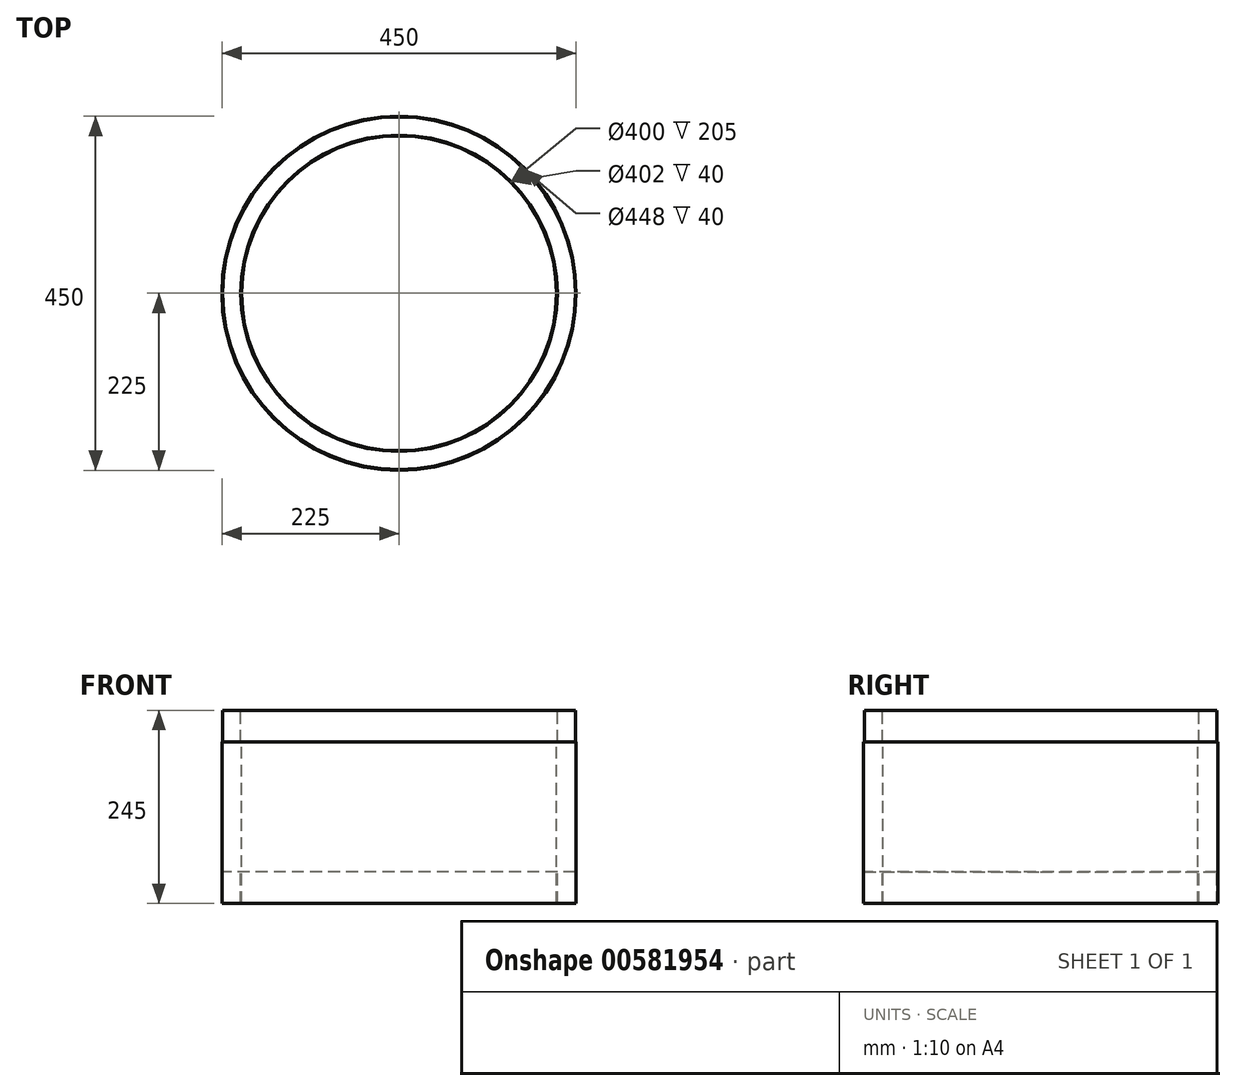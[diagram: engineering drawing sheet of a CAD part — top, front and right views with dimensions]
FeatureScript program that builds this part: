
annotation { "Feature Type Name" : "Feature", "Feature Type Description" : "" }
export const myFeature = defineFeature(function(context is Context, id is Id, definition is map)
    precondition{}
    {
        {
            var Q0;
            Q0=qCreatedBy(makeId("Front.planeOp"),FACE);
            var sketch = newSketch(context, id + "F0", { "sketchPlane" : qUnion([Q0])});
            skLineSegment(sketch, "E0", {"start": v(0, 345.75) * mm, "end": v(0, -558.03) * mm, "construction": true});
            skLineSegment(sketch, "E1", {"start": v(-200, -518.84) * mm, "end": v(-200, -313.84) * mm});
            skLineSegment(sketch, "E2", {"start": v(-200, -313.84) * mm, "end": v(-201, -313.84) * mm});
            skLineSegment(sketch, "E3", {"start": v(-201, -313.84) * mm, "end": v(-201, -273.84) * mm});
            skLineSegment(sketch, "E4", {"start": v(-201, -273.84) * mm, "end": v(-224, -273.84) * mm});
            skLineSegment(sketch, "E5", {"start": v(-224, -273.84) * mm, "end": v(-224, -313.84) * mm});
            skLineSegment(sketch, "E6", {"start": v(-224, -313.84) * mm, "end": v(-225, -313.84) * mm});
            skLineSegment(sketch, "E7", {"start": v(-225, -313.84) * mm, "end": v(-225, -518.84) * mm});
            skLineSegment(sketch, "E8", {"start": v(-225, -518.84) * mm, "end": v(-224, -518.84) * mm});
            skLineSegment(sketch, "E9", {"start": v(-224, -518.84) * mm, "end": v(-224, -478.84) * mm});
            skLineSegment(sketch, "E10", {"start": v(-224, -478.84) * mm, "end": v(-201, -478.84) * mm});
            skLineSegment(sketch, "E11", {"start": v(-201, -478.84) * mm, "end": v(-201, -518.84) * mm});
            skLineSegment(sketch, "E12", {"start": v(-201, -518.84) * mm, "end": v(-200, -518.84) * mm});
            skSolve(sketch);
        }
        {
            var Q0;
            Q0=qSketchRegion(id+"F0",true);
            var Q1;
            Q1=sQuery(id+"F0.wireOp",EDGE,"E0");
            revolve(context, id + "F1", {"entities" : qUnion([Q0]), "axis" : qUnion([Q1]), "revolveType" : RevolveType.FULL});
        }
    });
